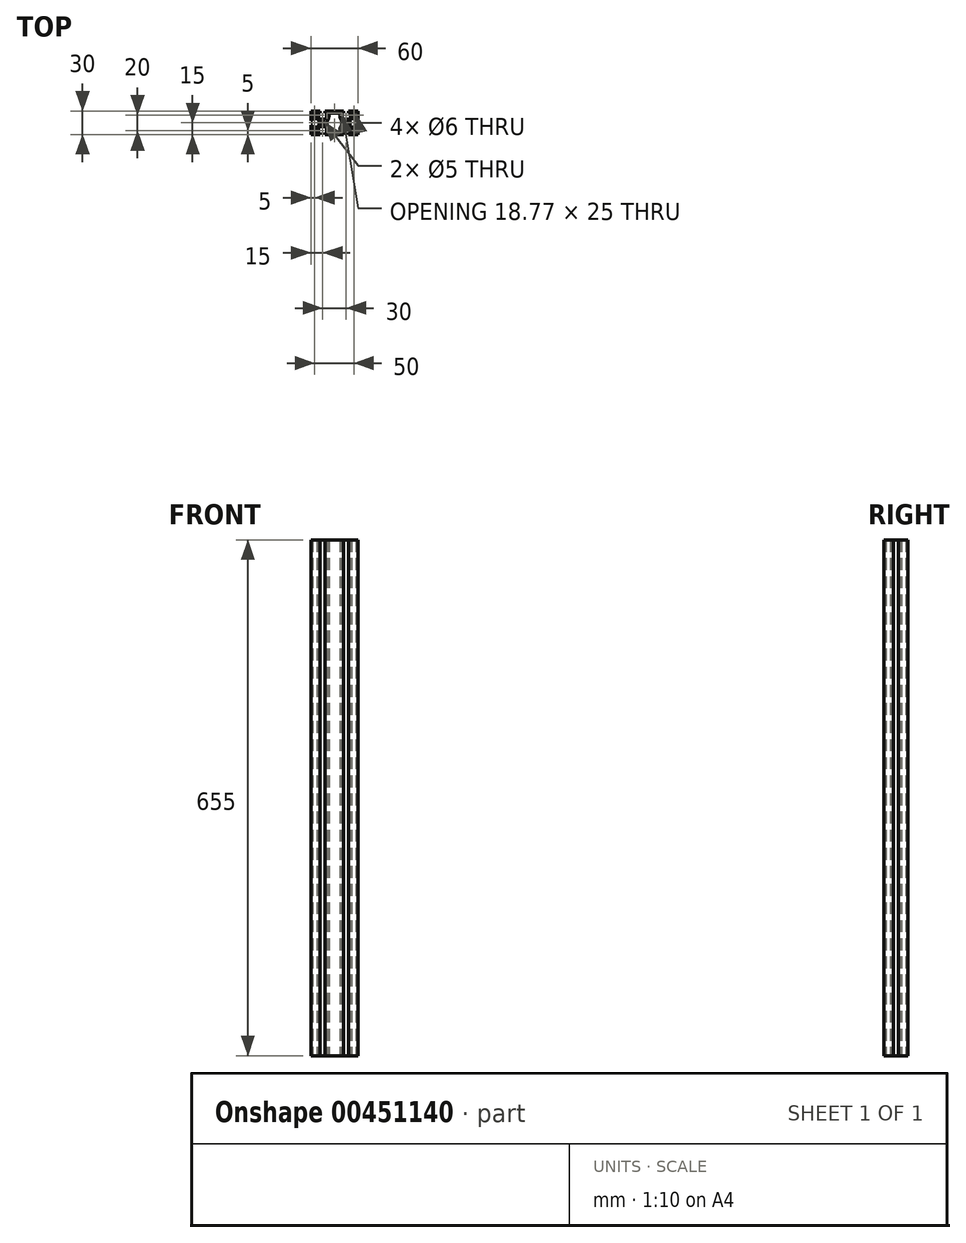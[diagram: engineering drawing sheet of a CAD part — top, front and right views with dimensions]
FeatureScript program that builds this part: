
annotation { "Feature Type Name" : "Feature", "Feature Type Description" : "" }
export const myFeature = defineFeature(function(context is Context, id is Id, definition is map)
    precondition{}
    {
        {
            var Q0;
            Q0=qCreatedBy(makeId("Top.planeOp"),FACE);
            var sketch = newSketch(context, id + "F0", { "sketchPlane" : qUnion([Q0])});
            skLineSegment(sketch, "E0.bottom", {"start": v(30, -15) * mm, "end": v(-30, -15) * mm});
            skLineSegment(sketch, "E0.top", {"start": v(30, 15) * mm, "end": v(-30, 15) * mm});
            skLineSegment(sketch, "E0.left", {"start": v(30, -15) * mm, "end": v(30, 15) * mm});
            skLineSegment(sketch, "E0.right", {"start": v(-30, -15) * mm, "end": v(-30, 15) * mm});
            skPoint(sketch, "E0.middle", {"position": v(0, 0) * mm});
            skLineSegment(sketch, "E1.top", {"start": v(-11.85, 15) * mm, "end": v(-18.15, 15) * mm});
            skLineSegment(sketch, "E1.left", {"start": v(-11.85, 12.5) * mm, "end": v(-11.85, 15) * mm});
            skLineSegment(sketch, "E1.right", {"start": v(-18.15, 12.5) * mm, "end": v(-18.15, 15) * mm});
            skPoint(sketch, "E1.middle", {"position": v(-15, 13.75) * mm});
            skLineSegment(sketch, "E2.bottom", {"start": v(-9.85, 12.5) * mm, "end": v(-11.85, 12.5) * mm});
            skLineSegment(sketch, "E2.left", {"start": v(-9.85, 12.5) * mm, "end": v(-9.85, 6.55) * mm});
            skLineSegment(sketch, "E2.right", {"start": v(-20.15, 12.5) * mm, "end": v(-20.15, 6.55) * mm});
            skPoint(sketch, "E2.middle", {"position": v(-15, 9.52) * mm});
            skArc(sketch, "E3", {"start": v(-20.15, 6.55) * mm, "mid": v(-15, 4.5) * mm, "end": v(-9.85, 6.55) * mm});
            skPoint(sketch, "E4.MirrorP", {"position": v(15, 9.52) * mm});
            skPoint(sketch, "E5.MirrorP", {"position": v(15, 13.75) * mm});
            skLineSegment(sketch, "E6.MirrorCS", {"start": v(11.85, 12.5) * mm, "end": v(11.85, 15) * mm});
            skLineSegment(sketch, "E7.MirrorCS", {"start": v(18.15, 12.5) * mm, "end": v(18.15, 15) * mm});
            skLineSegment(sketch, "E8.MirrorCS", {"start": v(9.85, 12.5) * mm, "end": v(11.85, 12.5) * mm});
            skLineSegment(sketch, "E9.MirrorCS", {"start": v(9.85, 12.5) * mm, "end": v(9.85, 6.55) * mm});
            skArc(sketch, "E10.MirrorCS", {"start": v(20.15, 6.55) * mm, "mid": v(15, 4.5) * mm, "end": v(9.85, 6.55) * mm});
            skLineSegment(sketch, "E11.MirrorCS", {"start": v(20.15, 12.5) * mm, "end": v(20.15, 6.55) * mm});
            skLineSegment(sketch, "E12.MirrorCS", {"start": v(11.85, 15) * mm, "end": v(18.15, 15) * mm});
            skLineSegment(sketch, "E13.trimOffspring", {"start": v(-18.15, 12.5) * mm, "end": v(-20.15, 12.5) * mm});
            skLineSegment(sketch, "E14.trimOffspring", {"start": v(18.15, 12.5) * mm, "end": v(20.15, 12.5) * mm});
            skCircle(sketch, "E15", {"center": v(-15, 0) * mm, "radius": 2.5 * mm});
            skCircle(sketch, "E16", {"center": v(-25, 10) * mm, "radius": 3 * mm});
            skCircle(sketch, "E17.MirrorC", {"center": v(25, 10) * mm, "radius": 3 * mm});
            skCircle(sketch, "E18.MirrorC", {"center": v(25, -10) * mm, "radius": 3 * mm});
            skCircle(sketch, "E19.MirrorC", {"center": v(-25, -10) * mm, "radius": 3 * mm});
            skCircle(sketch, "E20.MirrorC", {"center": v(15, 0) * mm, "radius": 2.5 * mm});
            skLineSegment(sketch, "E21", {"start": v(-7, 12.5) * mm, "end": v(0, 12.5) * mm});
            skLineSegment(sketch, "E22", {"start": v(-7, 12.5) * mm, "end": v(-7, 7) * mm});
            skLineSegment(sketch, "E23", {"start": v(-10, 0) * mm, "end": v(-7, 7) * mm});
            skLineSegment(sketch, "E24.MirrorCS", {"start": v(10, 0) * mm, "end": v(7, 7) * mm});
            skLineSegment(sketch, "E25.MirrorCS", {"start": v(7, 12.5) * mm, "end": v(0, 12.5) * mm});
            skLineSegment(sketch, "E26.MirrorCS", {"start": v(7, 12.5) * mm, "end": v(7, 7) * mm});
            skLineSegment(sketch, "E27.MirrorCS", {"start": v(-18.15, -12.5) * mm, "end": v(-20.15, -12.5) * mm});
            skLineSegment(sketch, "E28.MirrorCS", {"start": v(-9.85, -12.5) * mm, "end": v(-11.85, -12.5) * mm});
            skLineSegment(sketch, "E29.MirrorCS", {"start": v(-9.85, -12.5) * mm, "end": v(-9.85, -6.55) * mm});
            skPoint(sketch, "E30.MirrorP", {"position": v(-15, -13.75) * mm});
            skPoint(sketch, "E31.MirrorP", {"position": v(-15, -9.52) * mm});
            skLineSegment(sketch, "E32.MirrorCS", {"start": v(-18.15, -12.5) * mm, "end": v(-18.15, -15) * mm});
            skLineSegment(sketch, "E33.MirrorCS", {"start": v(-11.85, -15) * mm, "end": v(-18.15, -15) * mm});
            skLineSegment(sketch, "E34.MirrorCS", {"start": v(-20.15, -12.5) * mm, "end": v(-20.15, -6.55) * mm});
            skLineSegment(sketch, "E35.MirrorCS", {"start": v(-11.85, -12.5) * mm, "end": v(-11.85, -15) * mm});
            skArc(sketch, "E36.MirrorCS", {"start": v(-20.15, -6.55) * mm, "mid": v(-15, -4.5) * mm, "end": v(-9.85, -6.55) * mm});
            skLineSegment(sketch, "E37.MirrorCS", {"start": v(18.15, -12.5) * mm, "end": v(20.15, -12.5) * mm});
            skLineSegment(sketch, "E38.MirrorCS", {"start": v(9.85, -12.5) * mm, "end": v(11.85, -12.5) * mm});
            skPoint(sketch, "E39.MirrorP", {"position": v(15, -13.75) * mm});
            skPoint(sketch, "E40.MirrorP", {"position": v(15, -9.52) * mm});
            skLineSegment(sketch, "E41.MirrorCS", {"start": v(18.15, -12.5) * mm, "end": v(18.15, -15) * mm});
            skArc(sketch, "E42.MirrorCS", {"start": v(20.15, -6.55) * mm, "mid": v(15, -4.5) * mm, "end": v(9.85, -6.55) * mm});
            skLineSegment(sketch, "E43.MirrorCS", {"start": v(9.85, -12.5) * mm, "end": v(9.85, -6.55) * mm});
            skLineSegment(sketch, "E44.MirrorCS", {"start": v(11.85, -12.5) * mm, "end": v(11.85, -15) * mm});
            skLineSegment(sketch, "E45.MirrorCS", {"start": v(11.85, -15) * mm, "end": v(18.15, -15) * mm});
            skLineSegment(sketch, "E46.MirrorCS", {"start": v(20.15, -12.5) * mm, "end": v(20.15, -6.55) * mm});
            skLineSegment(sketch, "E47.MirrorCS", {"start": v(10, 0) * mm, "end": v(7, -7) * mm});
            skLineSegment(sketch, "E48.MirrorCS", {"start": v(7, -12.5) * mm, "end": v(7, -7) * mm});
            skLineSegment(sketch, "E49.MirrorCS", {"start": v(7, -12.5) * mm, "end": v(0, -12.5) * mm});
            skLineSegment(sketch, "E50.MirrorCS", {"start": v(-7, -12.5) * mm, "end": v(0, -12.5) * mm});
            skLineSegment(sketch, "E51.MirrorCS", {"start": v(-10, 0) * mm, "end": v(-7, -7) * mm});
            skLineSegment(sketch, "E52.MirrorCS", {"start": v(-7, -12.5) * mm, "end": v(-7, -7) * mm});
            skLineSegment(sketch, "E53.top", {"start": v(-30, 3.15) * mm, "end": v(-30, -3.15) * mm});
            skLineSegment(sketch, "E53.left", {"start": v(-27.5, 3.15) * mm, "end": v(-30, 3.15) * mm});
            skLineSegment(sketch, "E53.right", {"start": v(-27.5, -3.15) * mm, "end": v(-30, -3.15) * mm});
            skLineSegment(sketch, "E54.bottom", {"start": v(-27.5, 5.15) * mm, "end": v(-27.5, 3.15) * mm});
            skLineSegment(sketch, "E54.left", {"start": v(-27.5, 5.15) * mm, "end": v(-21.55, 5.15) * mm});
            skLineSegment(sketch, "E54.right", {"start": v(-27.5, -5.15) * mm, "end": v(-21.55, -5.15) * mm});
            skArc(sketch, "E55", {"start": v(-21.55, -5.15) * mm, "mid": v(-19.5, 0) * mm, "end": v(-21.55, 5.15) * mm});
            skLineSegment(sketch, "E56.trimOffspring", {"start": v(-27.5, -3.15) * mm, "end": v(-27.5, -5.15) * mm});
            skArc(sketch, "E57.MirrorCS", {"start": v(21.55, -5.15) * mm, "mid": v(19.5, 0) * mm, "end": v(21.55, 5.15) * mm});
            skLineSegment(sketch, "E58.MirrorCS", {"start": v(27.5, -5.15) * mm, "end": v(21.55, -5.15) * mm});
            skLineSegment(sketch, "E59.MirrorCS", {"start": v(30, 3.15) * mm, "end": v(30, -3.15) * mm});
            skLineSegment(sketch, "E60.MirrorCS", {"start": v(27.5, -3.15) * mm, "end": v(30, -3.15) * mm});
            skLineSegment(sketch, "E61.MirrorCS", {"start": v(27.5, 5.15) * mm, "end": v(27.5, 3.15) * mm});
            skLineSegment(sketch, "E62.MirrorCS", {"start": v(27.5, 3.15) * mm, "end": v(30, 3.15) * mm});
            skLineSegment(sketch, "E63.MirrorCS", {"start": v(27.5, 5.15) * mm, "end": v(21.55, 5.15) * mm});
            skLineSegment(sketch, "E64.MirrorCS", {"start": v(27.5, -3.15) * mm, "end": v(27.5, -5.15) * mm});
            skSolve(sketch);
        }
        {
            var Q0;
            {var subQ30=sQuery(id+"F0.wireOp",EDGE,"E1.left");Q0=makeQuery(id+"F0.imprint","IMPRINT",FACE,{"disambiguationData":[TD([[makeQuery(id+"F0.imprint","IMPRINT",EDGE,{"derivedFrom":subQ30}),-1.0]])]});}
            extrude(context, id + "F1", {"entities" : qUnion([Q0]), "depth" : 655 * mm});
        }
        {
            var Q0;
            Q0=makeQuery(id+"F1.opExtrude","SWEPT_EDGE",EDGE,{"disambiguationData":[OSD([sQuery(id+"F0.wireOp",EDGE,"E21"),sQuery(id+"F0.wireOp",EDGE,"E22")])]});
            var Q1;
            Q1=makeQuery(id+"F1.opExtrude","SWEPT_EDGE",EDGE,{"disambiguationData":[OSD([sQuery(id+"F0.wireOp",EDGE,"E25.MirrorCS"),sQuery(id+"F0.wireOp",EDGE,"E26.MirrorCS")])]});
            var Q2;
            Q2=makeQuery(id+"F1.opExtrude","SWEPT_EDGE",EDGE,{"disambiguationData":[OSD([sQuery(id+"F0.wireOp",EDGE,"840db5bc-c403-45cd-90c7-254e62d9e8c5.3.2"),sQuery(id+"F0.wireOp",EDGE,"840db5bc-c403-45cd-90c7-254e62d9e8c5.3.3")])]});
            var Q3;
            Q3=makeQuery(id+"F1.opExtrude","SWEPT_EDGE",EDGE,{"disambiguationData":[OSD([sQuery(id+"F0.wireOp",EDGE,"840db5bc-c403-45cd-90c7-254e62d9e8c5.3.4"),sQuery(id+"F0.wireOp",EDGE,"840db5bc-c403-45cd-90c7-254e62d9e8c5.3.5")])]});
            var Q4;
            Q4=makeQuery(id+"F1.opExtrude","SWEPT_EDGE",EDGE,{"disambiguationData":[OSD([sQuery(id+"F0.wireOp",EDGE,"840db5bc-c403-45cd-90c7-254e62d9e8c5.1.4"),sQuery(id+"F0.wireOp",EDGE,"840db5bc-c403-45cd-90c7-254e62d9e8c5.1.5")])]});
            var Q5;
            Q5=makeQuery(id+"F1.opExtrude","SWEPT_EDGE",EDGE,{"disambiguationData":[OSD([sQuery(id+"F0.wireOp",EDGE,"840db5bc-c403-45cd-90c7-254e62d9e8c5.1.2"),sQuery(id+"F0.wireOp",EDGE,"840db5bc-c403-45cd-90c7-254e62d9e8c5.1.3")])]});
            var Q6;
            Q6=makeQuery(id+"F1.opExtrude","SWEPT_EDGE",EDGE,{"disambiguationData":[OSD([sQuery(id+"F0.wireOp",EDGE,"840db5bc-c403-45cd-90c7-254e62d9e8c5.2.2"),sQuery(id+"F0.wireOp",EDGE,"840db5bc-c403-45cd-90c7-254e62d9e8c5.2.3")])]});
            var Q7;
            Q7=makeQuery(id+"F1.opExtrude","SWEPT_EDGE",EDGE,{"disambiguationData":[OSD([sQuery(id+"F0.wireOp",EDGE,"840db5bc-c403-45cd-90c7-254e62d9e8c5.2.4"),sQuery(id+"F0.wireOp",EDGE,"840db5bc-c403-45cd-90c7-254e62d9e8c5.2.5")])]});
            fillet(context, id + "F2", {"entities" : qUnion([Q0, Q1, Q2, Q3, Q4, Q5, Q6, Q7]), "radius" : 2 * mm, "tangentPropagation" : true, "allowEdgeOverflow" : false});
        }
        {
            var Q0;
            Q0=makeQuery(id+"F1.opExtrude","SWEPT_EDGE",EDGE,{"disambiguationData":[OSD([sQuery(id+"F0.wireOp",EDGE,"DFmKlNwq-wdCH-8nxe-YtyU-4GV9lN6q6mBF"),sQuery(id+"F0.wireOp",EDGE,"E23")])]});
            var Q1;
            Q1=makeQuery(id+"F1.opExtrude","SWEPT_EDGE",EDGE,{"disambiguationData":[OSD([sQuery(id+"F0.wireOp",EDGE,"666cdc41-9f22-4022-b962-67eb0134baf70.MirrorCS"),sQuery(id+"F0.wireOp",EDGE,"E24.MirrorCS")])]});
            var Q2;
            Q2=makeQuery(id+"F1.opExtrude","SWEPT_EDGE",EDGE,{"disambiguationData":[OSD([sQuery(id+"F0.wireOp",EDGE,"840db5bc-c403-45cd-90c7-254e62d9e8c5.3.0"),sQuery(id+"F0.wireOp",EDGE,"840db5bc-c403-45cd-90c7-254e62d9e8c5.3.1")])]});
            var Q3;
            Q3=makeQuery(id+"F1.opExtrude","SWEPT_EDGE",EDGE,{"disambiguationData":[OSD([sQuery(id+"F0.wireOp",EDGE,"840db5bc-c403-45cd-90c7-254e62d9e8c5.1.6"),sQuery(id+"F0.wireOp",EDGE,"840db5bc-c403-45cd-90c7-254e62d9e8c5.1.7")])]});
            var Q4;
            Q4=makeQuery(id+"F1.opExtrude","SWEPT_EDGE",EDGE,{"disambiguationData":[OSD([sQuery(id+"F0.wireOp",EDGE,"840db5bc-c403-45cd-90c7-254e62d9e8c5.1.0"),sQuery(id+"F0.wireOp",EDGE,"840db5bc-c403-45cd-90c7-254e62d9e8c5.1.1")])]});
            var Q5;
            Q5=makeQuery(id+"F1.opExtrude","SWEPT_EDGE",EDGE,{"disambiguationData":[OSD([sQuery(id+"F0.wireOp",EDGE,"840db5bc-c403-45cd-90c7-254e62d9e8c5.3.6"),sQuery(id+"F0.wireOp",EDGE,"840db5bc-c403-45cd-90c7-254e62d9e8c5.3.7")])]});
            var Q6;
            Q6=makeQuery(id+"F1.opExtrude","SWEPT_EDGE",EDGE,{"disambiguationData":[OSD([sQuery(id+"F0.wireOp",EDGE,"840db5bc-c403-45cd-90c7-254e62d9e8c5.2.0"),sQuery(id+"F0.wireOp",EDGE,"840db5bc-c403-45cd-90c7-254e62d9e8c5.2.1")])]});
            var Q7;
            Q7=makeQuery(id+"F1.opExtrude","SWEPT_EDGE",EDGE,{"disambiguationData":[OSD([sQuery(id+"F0.wireOp",EDGE,"840db5bc-c403-45cd-90c7-254e62d9e8c5.2.6"),sQuery(id+"F0.wireOp",EDGE,"840db5bc-c403-45cd-90c7-254e62d9e8c5.2.7")])]});
            fillet(context, id + "F3", {"entities" : qUnion([Q0, Q1, Q2, Q3, Q4, Q5, Q6, Q7]), "radius" : 7 * mm, "tangentPropagation" : true, "allowEdgeOverflow" : false});
        }
    });
